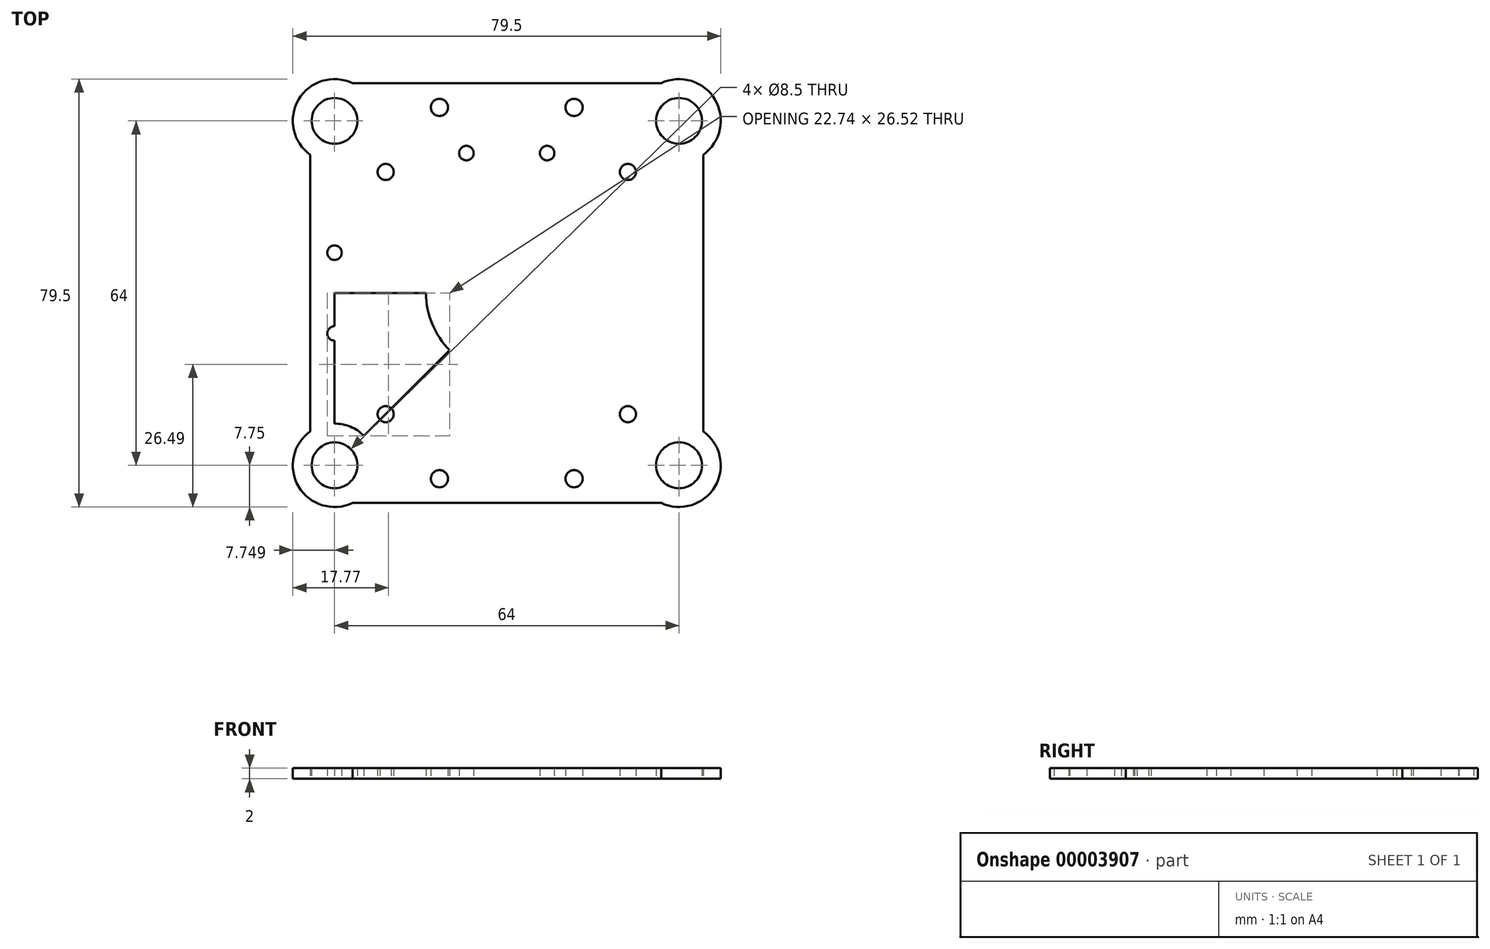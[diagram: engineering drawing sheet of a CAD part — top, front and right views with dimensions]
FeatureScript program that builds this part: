
annotation { "Feature Type Name" : "Feature", "Feature Type Description" : "" }
export const myFeature = defineFeature(function(context is Context, id is Id, definition is map)
    precondition{}
    {
        {
            var Q0;
            Q0=qCreatedBy(makeId("Top.planeOp"),FACE);
            var sketch = newSketch(context, id + "F0", { "sketchPlane" : qUnion([Q0])});
            skCircle(sketch, "E0", {"center": v(-37.11, 49.33) * mm, "radius": 4.25 * mm});
            skCircle(sketch, "E1", {"center": v(26.89, 49.33) * mm, "radius": 4.25 * mm});
            skCircle(sketch, "E2", {"center": v(-37.11, -14.67) * mm, "radius": 4.25 * mm});
            skCircle(sketch, "E3", {"center": v(26.89, -14.67) * mm, "radius": 4.25 * mm});
            skLineSegment(sketch, "E4", {"start": v(-37.11, 49.33) * mm, "end": v(26.89, -14.67) * mm});
            skLineSegment(sketch, "E5", {"start": v(26.89, 49.33) * mm, "end": v(-37.11, -14.67) * mm});
            skCircle(sketch, "E6", {"center": v(-27.61, 39.83) * mm, "radius": 1.5 * mm});
            skCircle(sketch, "E7", {"center": v(17.39, 39.83) * mm, "radius": 1.5 * mm});
            skCircle(sketch, "E8", {"center": v(17.39, -5.17) * mm, "radius": 1.5 * mm});
            skCircle(sketch, "E9", {"center": v(-27.61, -5.17) * mm, "radius": 1.5 * mm});
            skLineSegment(sketch, "E10", {"start": v(-37.11, 49.33) * mm, "end": v(-37.11, -14.67) * mm});
            skCircle(sketch, "E11", {"center": v(-37.11, 24.83) * mm, "radius": 1.35 * mm});
            skCircle(sketch, "E12", {"center": v(-37.11, 9.83) * mm, "radius": 1.35 * mm});
            skCircle(sketch, "E13", {"center": v(-37.11, 49.33) * mm, "radius": 7.75 * mm});
            skCircle(sketch, "E14", {"center": v(26.89, 49.33) * mm, "radius": 7.75 * mm});
            skCircle(sketch, "E15", {"center": v(-37.11, -14.67) * mm, "radius": 7.75 * mm});
            skCircle(sketch, "E16", {"center": v(26.89, -14.67) * mm, "radius": 7.75 * mm});
            skCircle(sketch, "E17", {"center": v(-17.61, -17.17) * mm, "radius": 1.6 * mm});
            skCircle(sketch, "E18", {"center": v(7.39, -17.17) * mm, "radius": 1.6 * mm});
            skLineSegment(sketch, "E19", {"start": v(-33.79, -21.67) * mm, "end": v(23.56, -21.67) * mm});
            skLineSegment(sketch, "E20", {"start": v(-55.65, 17.33) * mm, "end": v(63.27, 17.33) * mm});
            skPoint(sketch, "E21", {"position": v(-5.11, 17.33) * mm});
            skLineSegment(sketch, "E22.0.MirrorCS", {"start": v(-33.79, 56.33) * mm, "end": v(23.56, 56.33) * mm});
            skCircle(sketch, "E23.0.MirrorC", {"center": v(-17.61, 51.83) * mm, "radius": 1.6 * mm});
            skCircle(sketch, "E24.0.MirrorC", {"center": v(7.39, 51.83) * mm, "radius": 1.6 * mm});
            skLineSegment(sketch, "E25", {"start": v(-41.61, 45.56) * mm, "end": v(-41.61, -8.36) * mm});
            skLineSegment(sketch, "E26", {"start": v(-5.11, 56.33) * mm, "end": v(-5.11, -18.34) * mm});
            skLineSegment(sketch, "E27.0.MirrorCS", {"start": v(31.39, 43.02) * mm, "end": v(31.39, -8.36) * mm});
            skCircle(sketch, "E28", {"center": v(-5.11, 17.33) * mm, "radius": 15 * mm});
            skLineSegment(sketch, "E29", {"start": v(12.46, 43.33) * mm, "end": v(-24.81, 43.33) * mm});
            skCircle(sketch, "E30", {"center": v(-12.61, 43.33) * mm, "radius": 1.35 * mm});
            skCircle(sketch, "E31", {"center": v(2.39, 43.33) * mm, "radius": 1.35 * mm});
            skPoint(sketch, "E32", {"position": v(-5.11, 43.33) * mm});
            skSolve(sketch);
        }
        {
            var Q0;
            Q0 = qSketchRegion(id + "F0", true);
            var Q1;
            {var subQ8=sQuery(id+"F0.wireOp",EDGE,"E2");var subQ14=sQuery(id+"F0.wireOp",EDGE,"E5");var subQ20=makeQuery(id+"F0.imprint","INTERSECT",VERTEX,{"derivedFrom":[subQ8,subQ14]});Q1=makeQuery(id+"F0.imprint","IMPRINT",FACE,{"disambiguationData":[TD([[makeQuery(id+"F0.imprint","IMPRINT",EDGE,{"disambiguationData":[TD([[subQ20,-1.0]])],"derivedFrom":subQ8}),-1.0]])]});}
            var Q2;
            {var subQ3=sQuery(id+"F0.wireOp",EDGE,"E4");var subQ5=sQuery(id+"F0.wireOp",EDGE,"E0");var subQ7=makeQuery(id+"F0.imprint","INTERSECT",VERTEX,{"derivedFrom":[subQ5,subQ3]});Q2=makeQuery(id+"F0.imprint","IMPRINT",FACE,{"disambiguationData":[TD([[makeQuery(id+"F0.imprint","IMPRINT",EDGE,{"disambiguationData":[TD([[subQ7,1.0]])],"derivedFrom":subQ5}),-1.0]])]});}
            var Q3;
            {var subQ1=sQuery(id+"F0.wireOp",EDGE,"E4");var subQ5=sQuery(id+"F0.wireOp",EDGE,"E13");var subQ7=makeQuery(id+"F0.imprint","INTERSECT",VERTEX,{"derivedFrom":[subQ1,subQ5]});Q3=makeQuery(id+"F0.imprint","IMPRINT",FACE,{"disambiguationData":[TD([[makeQuery(id+"F0.imprint","IMPRINT",EDGE,{"disambiguationData":[TD([[subQ7,-1.0]])],"derivedFrom":subQ1}),-1.0]])]});}
            var Q4;
            {var subQ1=sQuery(id+"F0.wireOp",EDGE,"E5");var subQ10=sQuery(id+"F0.wireOp",EDGE,"E9");var subQ11=makeQuery(id+"F0.imprint","INTERSECT",VERTEX,{"disambiguationData":[OD(1.0)],"derivedFrom":[subQ1,subQ10]});Q4=makeQuery(id+"F0.imprint","IMPRINT",FACE,{"disambiguationData":[TD([[makeQuery(id+"F0.imprint","IMPRINT",EDGE,{"disambiguationData":[TD([[subQ11,-1.0]])],"derivedFrom":subQ1}),-1.0]])]});}
            var Q5;
            {var subQ0=sQuery(id+"F0.wireOp",EDGE,"E28");var subQ3=sQuery(id+"F0.wireOp",EDGE,"E4");var subQ4=makeQuery(id+"F0.imprint","INTERSECT",VERTEX,{"disambiguationData":[OD(0.0)],"derivedFrom":[subQ3,subQ0]});Q5=makeQuery(id+"F0.imprint","IMPRINT",FACE,{"disambiguationData":[TD([[makeQuery(id+"F0.imprint","IMPRINT",EDGE,{"disambiguationData":[TD([[subQ4,-1.0]])],"derivedFrom":subQ0}),1.0]])]});}
            var Q6;
            {var subQ0=sQuery(id+"F0.wireOp",EDGE,"E28");var subQ3=sQuery(id+"F0.wireOp",EDGE,"E26");var subQ4=makeQuery(id+"F0.imprint","INTERSECT",VERTEX,{"disambiguationData":[OD(0.0)],"derivedFrom":[subQ3,subQ0]});Q6=makeQuery(id+"F0.imprint","IMPRINT",FACE,{"disambiguationData":[TD([[makeQuery(id+"F0.imprint","IMPRINT",EDGE,{"disambiguationData":[TD([[subQ4,-1.0]])],"derivedFrom":subQ0}),1.0]])]});}
            var Q7;
            {var subQ0=sQuery(id+"F0.wireOp",EDGE,"E28");var subQ3=sQuery(id+"F0.wireOp",EDGE,"E26");var subQ4=makeQuery(id+"F0.imprint","INTERSECT",VERTEX,{"disambiguationData":[OD(0.0)],"derivedFrom":[subQ3,subQ0]});Q7=makeQuery(id+"F0.imprint","IMPRINT",FACE,{"disambiguationData":[TD([[makeQuery(id+"F0.imprint","IMPRINT",EDGE,{"disambiguationData":[TD([[subQ4,1.0]])],"derivedFrom":subQ0}),1.0]])]});}
            var Q8;
            {var subQ0=sQuery(id+"F0.wireOp",EDGE,"E28");var subQ3=sQuery(id+"F0.wireOp",EDGE,"E5");var subQ4=makeQuery(id+"F0.imprint","INTERSECT",VERTEX,{"disambiguationData":[OD(0.0)],"derivedFrom":[subQ3,subQ0]});Q8=makeQuery(id+"F0.imprint","IMPRINT",FACE,{"disambiguationData":[TD([[makeQuery(id+"F0.imprint","IMPRINT",EDGE,{"disambiguationData":[TD([[subQ4,1.0]])],"derivedFrom":subQ0}),1.0]])]});}
            var Q9;
            {var subQ0=sQuery(id+"F0.wireOp",EDGE,"E28");var subQ3=sQuery(id+"F0.wireOp",EDGE,"E4");var subQ4=makeQuery(id+"F0.imprint","INTERSECT",VERTEX,{"disambiguationData":[OD(1.0)],"derivedFrom":[subQ3,subQ0]});Q9=makeQuery(id+"F0.imprint","IMPRINT",FACE,{"disambiguationData":[TD([[makeQuery(id+"F0.imprint","IMPRINT",EDGE,{"disambiguationData":[TD([[subQ4,-1.0]])],"derivedFrom":subQ0}),1.0]])]});}
            var Q10;
            {var subQ0=sQuery(id+"F0.wireOp",EDGE,"E28");var subQ3=sQuery(id+"F0.wireOp",EDGE,"E26");var subQ4=makeQuery(id+"F0.imprint","INTERSECT",VERTEX,{"disambiguationData":[OD(1.0)],"derivedFrom":[subQ3,subQ0]});Q10=makeQuery(id+"F0.imprint","IMPRINT",FACE,{"disambiguationData":[TD([[makeQuery(id+"F0.imprint","IMPRINT",EDGE,{"disambiguationData":[TD([[subQ4,-1.0]])],"derivedFrom":subQ0}),1.0]])]});}
            var Q11;
            {var subQ0=sQuery(id+"F0.wireOp",EDGE,"E26");var subQ3=sQuery(id+"F0.wireOp",EDGE,"E28");var subQ4=makeQuery(id+"F0.imprint","INTERSECT",VERTEX,{"disambiguationData":[OD(1.0)],"derivedFrom":[subQ0,subQ3]});Q11=makeQuery(id+"F0.imprint","IMPRINT",FACE,{"disambiguationData":[TD([[makeQuery(id+"F0.imprint","IMPRINT",EDGE,{"disambiguationData":[TD([[subQ4,1.0]])],"derivedFrom":subQ3}),1.0]])]});}
            var Q12;
            {var subQ0=sQuery(id+"F0.wireOp",EDGE,"E28");var subQ3=sQuery(id+"F0.wireOp",EDGE,"E5");var subQ4=makeQuery(id+"F0.imprint","INTERSECT",VERTEX,{"disambiguationData":[OD(1.0)],"derivedFrom":[subQ3,subQ0]});Q12=makeQuery(id+"F0.imprint","IMPRINT",FACE,{"disambiguationData":[TD([[makeQuery(id+"F0.imprint","IMPRINT",EDGE,{"disambiguationData":[TD([[subQ4,1.0]])],"derivedFrom":subQ0}),1.0]])]});}
            extrude(context, id + "F1", {"entities" : qUnion([Q0, Q1, Q2, Q3, Q4, Q5, Q6, Q7, Q8, Q9, Q10, Q11, Q12]), "depth" : 2 * mm});
        }
    });
